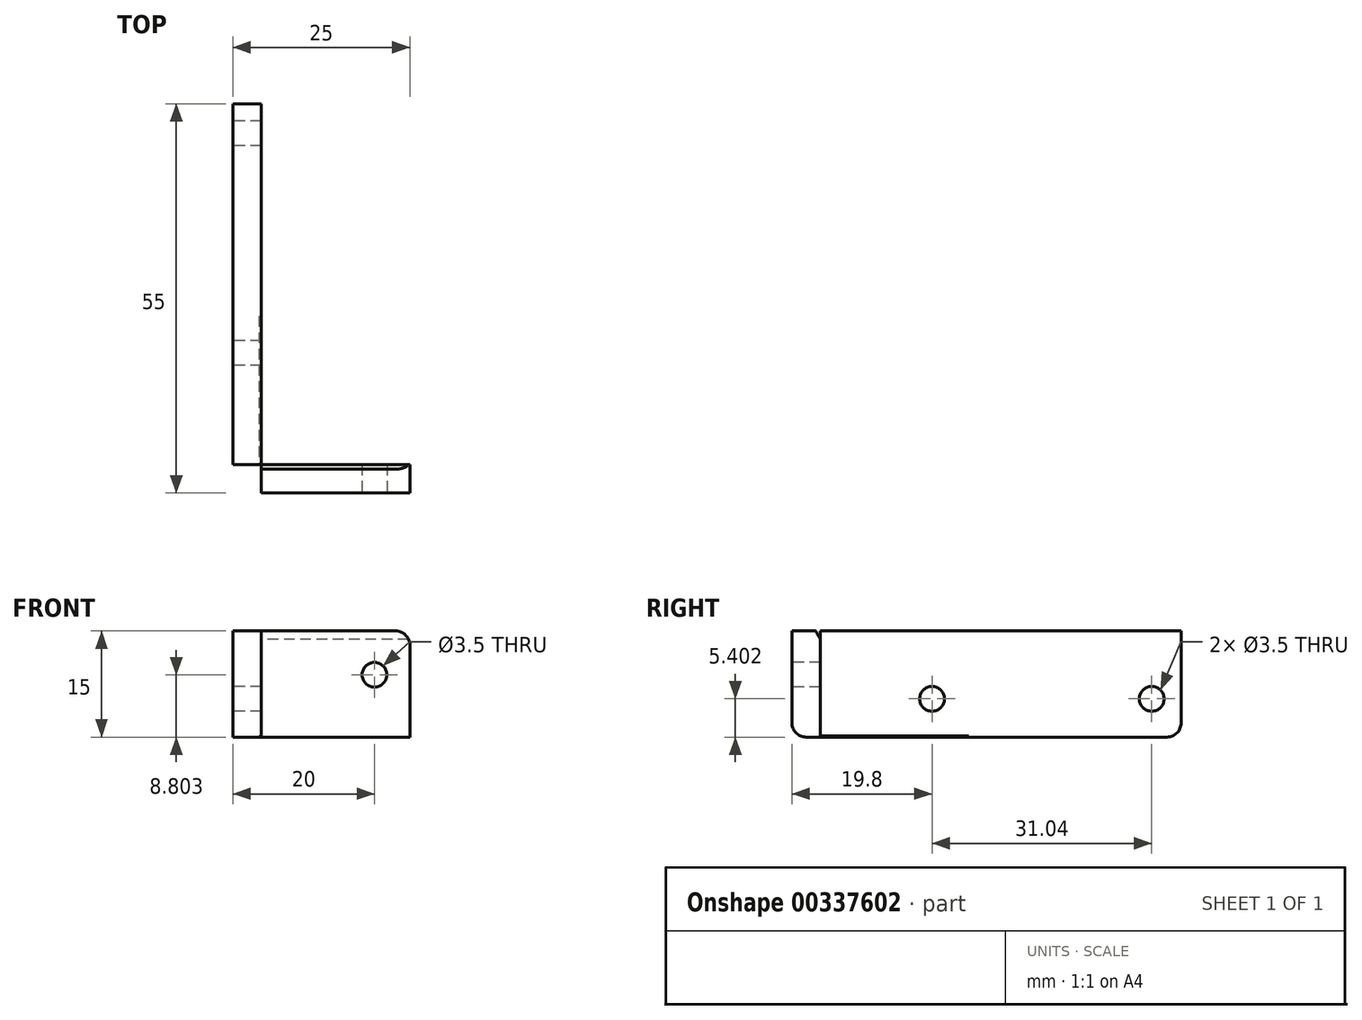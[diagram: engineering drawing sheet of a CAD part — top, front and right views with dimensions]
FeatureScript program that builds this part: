
annotation { "Feature Type Name" : "Feature", "Feature Type Description" : "" }
export const myFeature = defineFeature(function(context is Context, id is Id, definition is map)
    precondition{}
    {
        {
            var Q0;
            Q0=qCreatedBy(makeId("Top.planeOp"),FACE);
            var sketch = newSketch(context, id + "F0", { "sketchPlane" : qUnion([Q0])});
            skLineSegment(sketch, "E0.bottom", {"start": v(2, -27.5) * mm, "end": v(-2, -27.5) * mm});
            skLineSegment(sketch, "E0.top", {"start": v(2, 27.5) * mm, "end": v(-2, 27.5) * mm});
            skLineSegment(sketch, "E0.left", {"start": v(2, -27.5) * mm, "end": v(2, 27.5) * mm});
            skLineSegment(sketch, "E0.right", {"start": v(-2, -27.5) * mm, "end": v(-2, 27.5) * mm});
            skPoint(sketch, "E0.middle", {"position": v(0, 0) * mm});
            skLineSegment(sketch, "E1.bottom", {"start": v(-2, -27.5) * mm, "end": v(23, -27.5) * mm});
            skLineSegment(sketch, "E1.top", {"start": v(-2, -23.5) * mm, "end": v(23, -23.5) * mm});
            skLineSegment(sketch, "E1.left", {"start": v(-2, -27.5) * mm, "end": v(-2, -23.5) * mm});
            skLineSegment(sketch, "E1.right", {"start": v(23, -27.5) * mm, "end": v(23, -23.5) * mm});
            skSolve(sketch);
        }
        {
            var Q0;
            {var subQ0=sQuery(id+"F0.wireOp",EDGE,"E0.top");Q0=makeQuery(id+"F0.imprint","IMPRINT",FACE,{"disambiguationData":[TD([[makeQuery(id+"F0.imprint","IMPRINT",EDGE,{"derivedFrom":subQ0}),1.0]])]});}
            var Q1;
            {var subQ5=sQuery(id+"F0.wireOp",EDGE,"E1.left");Q1=makeQuery(id+"F0.imprint","IMPRINT",FACE,{"disambiguationData":[TD([[makeQuery(id+"F0.imprint","IMPRINT",EDGE,{"derivedFrom":subQ5}),-1.0]])]});}
            var Q2;
            {var subQ5=sQuery(id+"F0.wireOp",EDGE,"E1.right");Q2=makeQuery(id+"F0.imprint","IMPRINT",FACE,{"disambiguationData":[TD([[makeQuery(id+"F0.imprint","IMPRINT",EDGE,{"derivedFrom":subQ5}),1.0]])]});}
            extrude(context, id + "F1", {"entities" : qUnion([Q0, Q1, Q2]), "depth" : 15 * mm, "offsetDistance" : 25 * mm});
        }
        {
            var Q0;
            Q0=makeQuery(id+"F1.opExtrude","SWEPT_FACE",FACE,{"disambiguationData":[OSD([sQuery(id+"F0.wireOp",EDGE,"E0.right"),sQuery(id+"F0.wireOp",EDGE,"E1.left")])]});
            var sketch = newSketch(context, id + "F2", { "sketchPlane" : qUnion([Q0])});
            skLineSegment(sketch, "E2", {"start": v(-30.72, 5.4) * mm, "end": v(19.24, 5.4) * mm, "construction": true});
            skPoint(sketch, "E3", {"position": v(-23.34, 5.4) * mm});
            skPoint(sketch, "E4", {"position": v(7.7, 5.4) * mm});
            skLineSegment(sketch, "E5", {"start": v(-30.68, 10.34) * mm, "end": v(21.6, 10.34) * mm});
            skLineSegment(sketch, "E6", {"start": v(21.6, 10.34) * mm, "end": v(24.13, 15) * mm});
            skLineSegment(sketch, "E7", {"start": v(24.13, 15) * mm, "end": v(-27.5, 15) * mm});
            skLineSegment(sketch, "E8", {"start": v(-27.5, 15) * mm, "end": v(-27.5, 10.34) * mm});
            skSolve(sketch);
        }
        {
            var Q0;
            Q0=makeQuery(id+"F1.opExtrude","SWEPT_FACE",FACE,{"disambiguationData":[OSD([sQuery(id+"F0.wireOp",EDGE,"E1.bottom")])]});
            var sketch = newSketch(context, id + "F3", { "sketchPlane" : qUnion([Q0])});
            skLineSegment(sketch, "E9", {"start": v(-38.33, 8.8) * mm, "end": v(66.35, 8.8) * mm, "construction": true});
            skPoint(sketch, "E10", {"position": v(18, 8.8) * mm});
            skLineSegment(sketch, "E11", {"start": v(29.57, 4) * mm, "end": v(9.71, 4) * mm});
            skLineSegment(sketch, "E12", {"start": v(9.71, 4) * mm, "end": v(1.7, 0) * mm});
            skLineSegment(sketch, "E13", {"start": v(1.7, 0) * mm, "end": v(23, 0) * mm});
            skLineSegment(sketch, "E14", {"start": v(23, 0) * mm, "end": v(23, 4) * mm});
            skSolve(sketch);
        }
        {
            var Q0;
            Q0=sQuery(id+"F2.wireOp",VERTEX,"E3");
            var Q1;
            Q1=sQuery(id+"F2.wireOp",VERTEX,"E4");
            var Q2;
            Q2=sQuery(id+"F3.wireOp",VERTEX,"E10");
            var Q3;
            Q3=makeQuery(id+"F1.opExtrude","SWEPT_BODY",BODY,{"disambiguationData":[OSD([sQuery(id+"F0.wireOp",EDGE,"E0.top"),sQuery(id+"F0.wireOp",EDGE,"E0.left"),sQuery(id+"F0.wireOp",EDGE,"E0.right"),sQuery(id+"F0.wireOp",EDGE,"E1.bottom"),sQuery(id+"F0.wireOp",EDGE,"E1.top"),sQuery(id+"F0.wireOp",EDGE,"E1.left"),sQuery(id+"F0.wireOp",EDGE,"E1.right")])]});
            hole(context, id + "F4", {"style" : HoleStyle.SIMPLE, "endStyle" : HoleEndStyle.THROUGH, "holeDiameter" : 3.5 * mm, "tappedDepth" : 12 * mm, "tapClearance" : 3, "locations" : qUnion([Q0, Q1, Q2]), "scope" : qUnion([Q3])});
        }
        {
            var Q0;
            {var subQ0=sQuery(id+"F2.wireOp",EDGE,"E6");Q0=makeQuery(id+"F2.imprint","IMPRINT",FACE,{"disambiguationData":[TD([[makeQuery(id+"F2.imprint","IMPRINT",EDGE,{"derivedFrom":subQ0}),1.0]])]});}
            extrude(context, id + "F5", {"entities" : qUnion([Q0]), "operationType" : NewBodyOperationType.REMOVE, "oppositeDirection" : true, "depth" : 25 * mm, "offsetDistance" : 25 * mm});
        }
        {
            var Q0;
            {var subQ0=sQuery(id+"F3.wireOp",EDGE,"E12");Q0=makeQuery(id+"F3.imprint","IMPRINT",FACE,{"disambiguationData":[TD([[makeQuery(id+"F3.imprint","IMPRINT",EDGE,{"derivedFrom":subQ0}),1.0]])]});}
            extrude(context, id + "F6", {"entities" : qUnion([Q0]), "operationType" : NewBodyOperationType.REMOVE, "oppositeDirection" : true, "depth" : 25 * mm});
        }
        {
            var Q0;
            Q0=makeQuery(id+"F5.boolean.opBoolean","COPY",EDGE,{"derivedFrom":makeQuery(id+"F5.opExtrude","SWEPT_EDGE",EDGE,{"disambiguationData":[OSD([sQuery(id+"F0.wireOp",EDGE,"E0.top"),sQuery(id+"F0.wireOp",EDGE,"E0.right"),sQuery(id+"F2.wireOp",EDGE,"E5"),sQuery(id+"F2.wireOp",EDGE,"E8")])]})});
            var Q1;
            Q1=makeQuery(id+"F1.opExtrude","CAP_EDGE",EDGE,{"disambiguationData":[OSD([sQuery(id+"F0.wireOp",EDGE,"E0.top")])],"isStart":true});
            var Q2;
            Q2=makeQuery(id+"F1.opExtrude","CAP_EDGE",EDGE,{"disambiguationData":[OSD([sQuery(id+"F0.wireOp",EDGE,"E1.right")])],"isStart":false});
            var Q3;
            Q3=makeQuery(id+"F6.boolean.opBoolean","COPY",EDGE,{"derivedFrom":makeQuery(id+"F6.opExtrude","SWEPT_EDGE",EDGE,{"disambiguationData":[OSD([sQuery(id+"F0.wireOp",EDGE,"E1.bottom"),sQuery(id+"F0.wireOp",EDGE,"E1.right"),sQuery(id+"F3.wireOp",EDGE,"E11"),sQuery(id+"F3.wireOp",EDGE,"E14")])]})});
            var Q4;
            Q4=makeQuery(id+"F6.boolean.opBoolean","COPY",EDGE,{"derivedFrom":makeQuery(id+"F6.opExtrude","SWEPT_EDGE",EDGE,{"disambiguationData":[OSD([sQuery(id+"F3.wireOp",EDGE,"E11"),sQuery(id+"F3.wireOp",EDGE,"E12")])]})});
            var Q5;
            Q5=makeQuery(id+"F5.boolean.opBoolean","COPY",EDGE,{"derivedFrom":makeQuery(id+"F5.opExtrude","SWEPT_EDGE",EDGE,{"disambiguationData":[OSD([sQuery(id+"F0.wireOp",EDGE,"E0.right"),sQuery(id+"F0.wireOp",EDGE,"E1.left"),sQuery(id+"F2.wireOp",EDGE,"E6"),sQuery(id+"F2.wireOp",EDGE,"E7")])]})});
            var Q6;
            Q6=makeQuery(id+"F1.opExtrude","CAP_EDGE",EDGE,{"disambiguationData":[OSD([sQuery(id+"F0.wireOp",EDGE,"E1.bottom")])],"isStart":true});
            fillet(context, id + "F7", {"entities" : qUnion([Q0, Q1, Q2, Q3, Q4, Q5, Q6]), "radius" : 2 * mm, "tangentPropagation" : true, "allowEdgeOverflow" : false});
        }
    });
